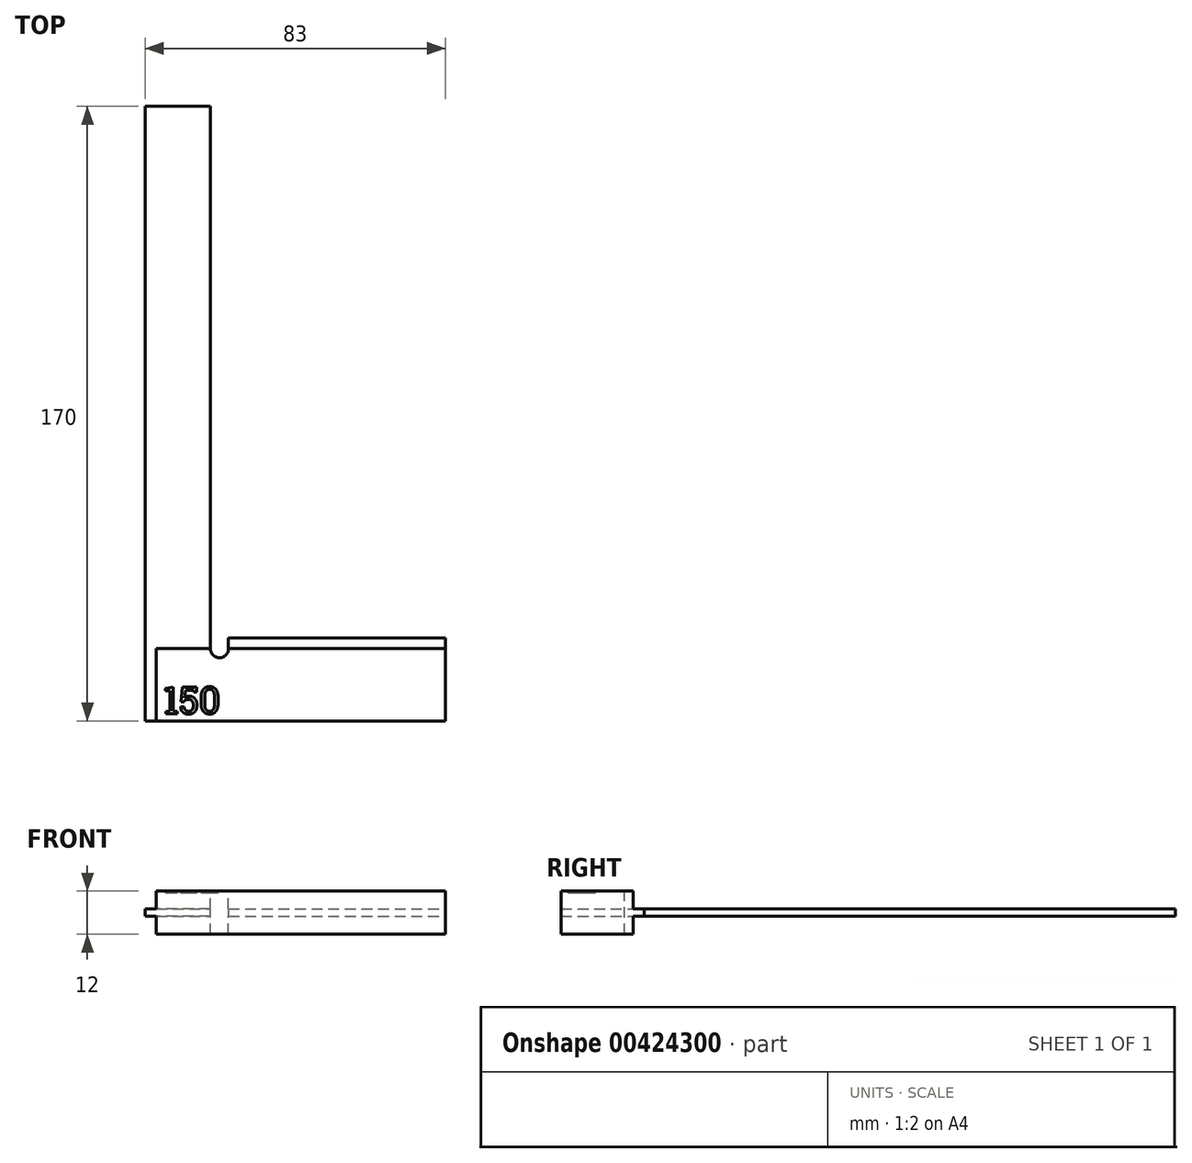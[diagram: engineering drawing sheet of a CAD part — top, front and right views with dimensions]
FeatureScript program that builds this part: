
annotation { "Feature Type Name" : "Feature", "Feature Type Description" : "" }
export const myFeature = defineFeature(function(context is Context, id is Id, definition is map)
    precondition{}
    {
        {
            var Q0;
            Q0=qCreatedBy(makeId("Top.planeOp"),FACE);
            var sketch = newSketch(context, id + "F0", { "sketchPlane" : qUnion([Q0])});
            skLineSegment(sketch, "E0.bottom", {"start": v(0, 0) * mm, "end": v(80, 0) * mm});
            skLineSegment(sketch, "E0.top", {"start": v(0, 20) * mm, "end": v(80, 20) * mm});
            skLineSegment(sketch, "E0.left", {"start": v(0, 0) * mm, "end": v(0, 20) * mm});
            skLineSegment(sketch, "E0.right", {"start": v(80, 0) * mm, "end": v(80, 20) * mm});
            skSolve(sketch);
        }
        {
            var Q0;
            Q0=qSketchRegion(id+"F0",true);
            extrude(context, id + "F1", {"entities" : qUnion([Q0]), "depth" : 12 * mm});
        }
        {
            var Q0;
            Q0=makeQuery(id+"F1.opExtrude","SWEPT_FACE",FACE,{"disambiguationData":[OSD([sQuery(id+"F0.wireOp",EDGE,"E0.top")])]});
            var sketch = newSketch(context, id + "F2", { "sketchPlane" : qUnion([Q0])});
            skLineSegment(sketch, "E1", {"start": v(-80, 6) * mm, "end": v(0, 6) * mm, "construction": true});
            skPoint(sketch, "E2", {"position": v(-15, 6) * mm});
            skLineSegment(sketch, "E3.bottom", {"start": v(-15, 5) * mm, "end": v(-80, 5) * mm});
            skLineSegment(sketch, "E3.top", {"start": v(-15, 7) * mm, "end": v(-80, 7) * mm});
            skLineSegment(sketch, "E3.right", {"start": v(-80, 5) * mm, "end": v(-80, 7) * mm});
            skPoint(sketch, "E3.middle", {"position": v(-40, 6) * mm});
            skLineSegment(sketch, "E4", {"start": v(-15, 7) * mm, "end": v(-15, 5) * mm});
            skSolve(sketch);
        }
        {
            var Q0;
            Q0=qSketchRegion(id+"F2",true);
            extrude(context, id + "F3", {"entities" : qUnion([Q0]), "operationType" : NewBodyOperationType.ADD, "depth" : 3 * mm});
        }
        {
            var Q0;
            Q0=makeQuery(id+"F1.opExtrude","SWEPT_FACE",FACE,{"disambiguationData":[OSD([sQuery(id+"F0.wireOp",EDGE,"E0.top")])]});
            var sketch = newSketch(context, id + "F4", { "sketchPlane" : qUnion([Q0])});
            skLineSegment(sketch, "E5", {"start": v(-15, 6) * mm, "end": v(0, 6) * mm, "construction": true});
            skLineSegment(sketch, "E6.bottom", {"start": v(-15, 5) * mm, "end": v(3, 5) * mm});
            skLineSegment(sketch, "E6.top", {"start": v(-15, 7) * mm, "end": v(3, 7) * mm});
            skLineSegment(sketch, "E6.left", {"start": v(-15, 5) * mm, "end": v(-15, 7) * mm});
            skPoint(sketch, "E6.middle", {"position": v(-6, 6) * mm});
            skLineSegment(sketch, "E7", {"start": v(3, 7) * mm, "end": v(3, 5) * mm});
            skSolve(sketch);
        }
        {
            var Q0;
            Q0=qSketchRegion(id+"F4",true);
            var Q1;
            Q1=makeQuery(id+"F1.opExtrude","SWEPT_FACE",FACE,{"disambiguationData":[OSD([sQuery(id+"F0.wireOp",EDGE,"E0.bottom")])]});
            extrude(context, id + "F5", {"entities" : qUnion([Q0]), "operationType" : NewBodyOperationType.ADD, "depth" : 150 * mm, "hasSecondDirection" : true, "secondDirectionBound" : SecondDirectionBoundingType.UP_TO_SURFACE, "secondDirectionOppositeDirection" : true, "secondDirectionBoundEntityFace" : qUnion([Q1]), "secondDirectionDepth" : 25 * mm});
        }
        {
            var Q0;
            Q0=qCreatedBy(makeId("Top.planeOp"),FACE);
            var sketch = newSketch(context, id + "F6", { "sketchPlane" : qUnion([Q0])});
            skPoint(sketch, "E8.0", {"position": v(15, 20) * mm});
            skLineSegment(sketch, "E9.0", {"start": v(80, 20) * mm, "end": v(0, 20) * mm, "construction": true});
            skArc(sketch, "E10", {"start": v(15, 20) * mm, "mid": v(17.5, 17.5) * mm, "end": v(20, 20) * mm});
            skLineSegment(sketch, "E11", {"start": v(20, 20) * mm, "end": v(20, 25.7) * mm});
            skLineSegment(sketch, "E12", {"start": v(20, 25.7) * mm, "end": v(15, 25.7) * mm});
            skLineSegment(sketch, "E13", {"start": v(15, 25.7) * mm, "end": v(15, 20) * mm});
            skSolve(sketch);
        }
        {
            var Q0;
            Q0=qSketchRegion(id+"F6",true);
            extrude(context, id + "F7", {"entities" : qUnion([Q0]), "operationType" : NewBodyOperationType.REMOVE, "endBound" : BoundingType.SYMMETRIC, "oppositeDirection" : true, "depth" : 25 * mm});
        }
        {
            var Q0;
            Q0=makeQuery(id+"F1.opExtrude","CAP_FACE",FACE,{"disambiguationData":[OSD([sQuery(id+"F0.wireOp",EDGE,"E0.bottom"),sQuery(id+"F0.wireOp",EDGE,"E0.top"),sQuery(id+"F0.wireOp",EDGE,"E0.left"),sQuery(id+"F0.wireOp",EDGE,"E0.right")])],"isStart":false});
            var sketch = newSketch(context, id + "F8", { "sketchPlane" : qUnion([Q0])});
            skText(sketch, "E14", { "text": "150", "fontName": "RobotoSlab-Regular.ttf"});
            const initialGuessF8  = {"E14": [0.002, 0.002, 1, 0, 0.0075]};
            skSetInitialGuess(sketch, initialGuessF8);
            skSolve(sketch);
        }
        {
            var Q0;
            Q0=qSketchRegion(id+"F8",true);
            extrude(context, id + "F9", {"entities" : qUnion([Q0]), "operationType" : NewBodyOperationType.REMOVE, "oppositeDirection" : true, "depth" : 0.5 * mm});
        }
    });
